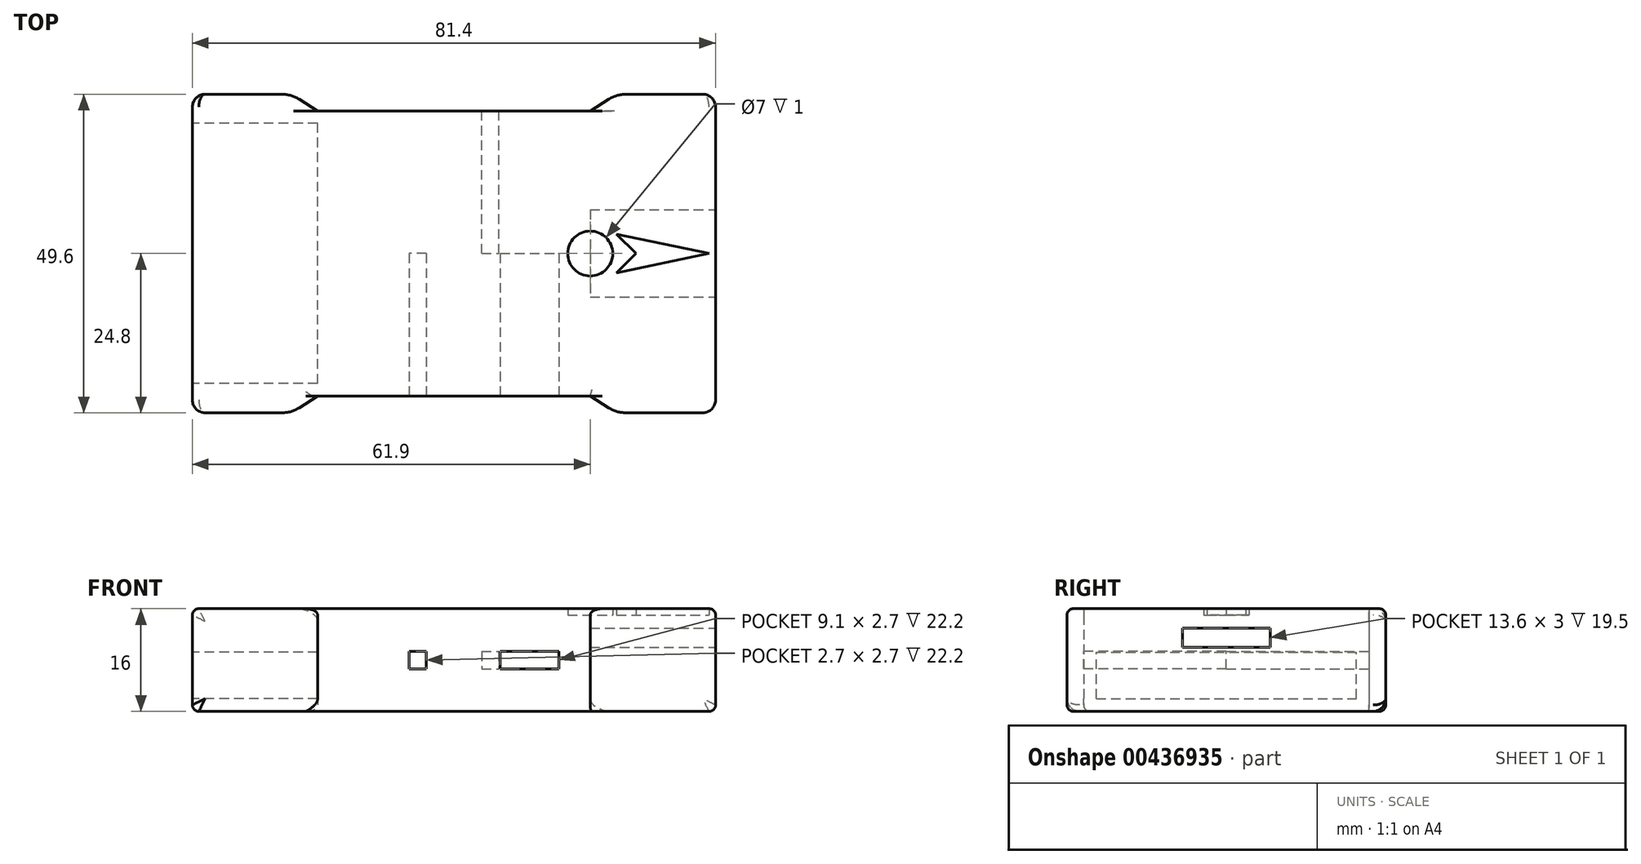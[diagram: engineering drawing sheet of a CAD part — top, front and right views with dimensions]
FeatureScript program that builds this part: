
annotation { "Feature Type Name" : "Feature", "Feature Type Description" : "" }
export const myFeature = defineFeature(function(context is Context, id is Id, definition is map)
    precondition{}
    {
        {
            var Q0;
            Q0=qCreatedBy(makeId("Front.planeOp"),FACE);
            cPlane(context, id + "F0", {"entities" : qUnion([Q0]), "cplaneType" : CPlaneType.OFFSET, "offset" : 22.2 * mm, "width" : 150 * mm, "height" : 150 * mm});
        }
        {
            var Q0;
            Q0=qCreatedBy(makeId("Front.planeOp"),FACE);
            cPlane(context, id + "F1", {"entities" : qUnion([Q0]), "cplaneType" : CPlaneType.OFFSET, "offset" : 22.2 * mm, "oppositeDirection" : true, "width" : 150 * mm, "height" : 150 * mm});
        }
        {
            var Q0;
            Q0=qCreatedBy(makeId("Right.planeOp"),FACE);
            cPlane(context, id + "F2", {"entities" : qUnion([Q0]), "cplaneType" : CPlaneType.OFFSET, "offset" : 40.7 * mm, "width" : 150 * mm, "height" : 150 * mm});
        }
        {
            var Q0;
            Q0=qCreatedBy(makeId("Right.planeOp"),FACE);
            cPlane(context, id + "F3", {"entities" : qUnion([Q0]), "cplaneType" : CPlaneType.OFFSET, "offset" : 40.7 * mm, "oppositeDirection" : true, "width" : 150 * mm, "height" : 150 * mm});
        }
        {
            var Q0;
            Q0=qCreatedBy(makeId("Top.planeOp"),FACE);
            cPlane(context, id + "F4", {"entities" : qUnion([Q0]), "cplaneType" : CPlaneType.OFFSET, "offset" : 13 * mm, "width" : 150 * mm, "height" : 150 * mm});
        }
        {
            var Q0;
            Q0=qCreatedBy(makeId("Top.planeOp"),FACE);
            cPlane(context, id + "F5", {"entities" : qUnion([Q0]), "cplaneType" : CPlaneType.OFFSET, "offset" : 15 * mm, "width" : 150 * mm, "height" : 150 * mm});
        }
        {
            var Q0;
            Q0=qCreatedBy(makeId("Top.planeOp"),FACE);
            var sketch = newSketch(context, id + "F6", { "sketchPlane" : qUnion([Q0])});
            skLineSegment(sketch, "E0.bottom", {"start": v(40.7, -24.8) * mm, "end": v(-40.7, -24.8) * mm, "construction": true});
            skLineSegment(sketch, "E0.top", {"start": v(40.7, 24.8) * mm, "end": v(-40.7, 24.8) * mm, "construction": true});
            skLineSegment(sketch, "E0.left", {"start": v(40.7, -24.8) * mm, "end": v(40.7, 24.8) * mm});
            skLineSegment(sketch, "E0.right", {"start": v(-40.7, -24.8) * mm, "end": v(-40.7, 24.8) * mm});
            skPoint(sketch, "E0.middle", {"position": v(0, 0) * mm});
            skLineSegment(sketch, "E1.bottom", {"start": v(-40.7, 22.2) * mm, "end": v(40.7, 22.2) * mm, "construction": true});
            skLineSegment(sketch, "E1.top", {"start": v(-40.7, -22.2) * mm, "end": v(40.7, -22.2) * mm, "construction": true});
            skLineSegment(sketch, "E2.0", {"start": v(-25.3, -24.8) * mm, "end": v(-25.3, 24.8) * mm, "construction": true});
            skLineSegment(sketch, "E3.0", {"start": v(-21.2, -24.8) * mm, "end": v(-21.2, 24.8) * mm, "construction": true});
            skLineSegment(sketch, "E4", {"start": v(0, 24.8) * mm, "end": v(0, -24.8) * mm, "construction": true});
            skLineSegment(sketch, "E5.MirrorCS", {"start": v(21.2, -24.8) * mm, "end": v(21.2, 24.8) * mm, "construction": true});
            skLineSegment(sketch, "E6.MirrorCS", {"start": v(25.3, -24.8) * mm, "end": v(25.3, 24.8) * mm, "construction": true});
            skLineSegment(sketch, "E7", {"start": v(-25.3, 24.8) * mm, "end": v(-21.2, 22.2) * mm});
            skLineSegment(sketch, "E8", {"start": v(-21.2, 22.2) * mm, "end": v(21.2, 22.2) * mm});
            skLineSegment(sketch, "E9", {"start": v(21.2, 22.2) * mm, "end": v(25.3, 24.8) * mm});
            skLineSegment(sketch, "E10", {"start": v(25.3, 24.8) * mm, "end": v(40.7, 24.8) * mm});
            skLineSegment(sketch, "E11", {"start": v(-25.3, 24.8) * mm, "end": v(-40.7, 24.8) * mm});
            skLineSegment(sketch, "E12", {"start": v(-40.7, -24.8) * mm, "end": v(-25.3, -24.8) * mm});
            skLineSegment(sketch, "E13", {"start": v(-25.3, -24.8) * mm, "end": v(-21.2, -22.2) * mm});
            skLineSegment(sketch, "E14", {"start": v(-21.2, -22.2) * mm, "end": v(21.2, -22.2) * mm});
            skLineSegment(sketch, "E15", {"start": v(21.2, -22.2) * mm, "end": v(25.3, -24.8) * mm});
            skLineSegment(sketch, "E16", {"start": v(25.3, -24.8) * mm, "end": v(40.7, -24.8) * mm});
            skLineSegment(sketch, "E17", {"start": v(-21.2, 22.2) * mm, "end": v(-40.7, 22.2) * mm});
            skLineSegment(sketch, "E18", {"start": v(21.2, 22.2) * mm, "end": v(40.7, 22.2) * mm});
            skLineSegment(sketch, "E19", {"start": v(21.2, -22.2) * mm, "end": v(40.7, -22.2) * mm});
            skLineSegment(sketch, "E20", {"start": v(-21.2, -22.2) * mm, "end": v(-40.7, -22.2) * mm});
            skCircle(sketch, "E21", {"center": v(0, 0) * mm, "radius": 0.5 * mm, "construction": true});
            skSolve(sketch);
        }
        {
            var Q0;
            Q0=qCreatedBy(id+"F0.planeOp",FACE);
            var sketch = newSketch(context, id + "F7", { "sketchPlane" : qUnion([Q0])});
            skLineSegment(sketch, "E22.3", {"start": v(40.7, 0) * mm, "end": v(40.7, 16) * mm});
            skLineSegment(sketch, "E22.6", {"start": v(-40.7, 0) * mm, "end": v(-40.7, 16) * mm});
            skCircle(sketch, "E23", {"center": v(0, 16) * mm, "radius": 0.5 * mm, "construction": true});
            skLineSegment(sketch, "E24", {"start": v(40.7, 0) * mm, "end": v(-40.7, 0) * mm});
            skLineSegment(sketch, "E25", {"start": v(-40.7, 16) * mm, "end": v(40.7, 16) * mm});
            skLineSegment(sketch, "E26", {"start": v(-4.3, 6.65) * mm, "end": v(-7, 6.65) * mm});
            skLineSegment(sketch, "E27.0", {"start": v(-4.3, 9.35) * mm, "end": v(-7, 9.35) * mm});
            skLineSegment(sketch, "E28", {"start": v(-4.3, 6.65) * mm, "end": v(-4.3, 9.35) * mm});
            skLineSegment(sketch, "E29", {"start": v(-7, 6.65) * mm, "end": v(-7, 9.35) * mm});
            skLineSegment(sketch, "E30.0", {"start": v(16.3, 6.65) * mm, "end": v(16.3, 9.35) * mm});
            skLineSegment(sketch, "E31.0", {"start": v(7.2, 6.65) * mm, "end": v(7.2, 9.35) * mm});
            skLineSegment(sketch, "E32", {"start": v(7.2, 6.65) * mm, "end": v(16.3, 6.65) * mm});
            skLineSegment(sketch, "E33", {"start": v(7.2, 9.35) * mm, "end": v(16.3, 9.35) * mm});
            skLineSegment(sketch, "E34.0", {"start": v(21.2, 0) * mm, "end": v(21.2, 16) * mm});
            skLineSegment(sketch, "E35.0", {"start": v(-21.2, 0) * mm, "end": v(-21.2, 16) * mm});
            skLineSegment(sketch, "E36", {"start": v(0, 16) * mm, "end": v(0, 0) * mm, "construction": true});
            skCircle(sketch, "E37", {"center": v(0, 0) * mm, "radius": 0.5 * mm, "construction": true});
            skSolve(sketch);
        }
        {
            var Q0;
            Q0=qCreatedBy(id+"F1.planeOp",FACE);
            var sketch = newSketch(context, id + "F8", { "sketchPlane" : qUnion([Q0])});
            skLineSegment(sketch, "E38.3", {"start": v(-40.7, 16) * mm, "end": v(-40.7, 0) * mm});
            skLineSegment(sketch, "E38.6", {"start": v(40.7, 16) * mm, "end": v(40.7, 0) * mm});
            skLineSegment(sketch, "E39", {"start": v(-40.7, 16) * mm, "end": v(40.7, 16) * mm});
            skLineSegment(sketch, "E40", {"start": v(40.7, 0) * mm, "end": v(-40.7, 0) * mm});
            skLineSegment(sketch, "E41", {"start": v(4.3, 9.35) * mm, "end": v(7, 9.35) * mm});
            skLineSegment(sketch, "E42.0", {"start": v(4.3, 6.65) * mm, "end": v(7, 6.65) * mm});
            skLineSegment(sketch, "E43", {"start": v(4.3, 9.35) * mm, "end": v(4.3, 6.65) * mm});
            skLineSegment(sketch, "E44", {"start": v(7, 9.35) * mm, "end": v(7, 6.65) * mm});
            skCircle(sketch, "E45", {"center": v(0, 16) * mm, "radius": 0.5 * mm, "construction": true});
            skLineSegment(sketch, "E46.0", {"start": v(21.2, 0) * mm, "end": v(21.2, 16) * mm});
            skLineSegment(sketch, "E47.0", {"start": v(-21.2, 0) * mm, "end": v(-21.2, 16) * mm});
            skLineSegment(sketch, "E48", {"start": v(0, 16) * mm, "end": v(0, 0) * mm, "construction": true});
            skCircle(sketch, "E49", {"center": v(0, 0) * mm, "radius": 0.5 * mm, "construction": true});
            skSolve(sketch);
        }
        {
            var Q0;
            Q0=qCreatedBy(id+"F2.planeOp",FACE);
            var sketch = newSketch(context, id + "F9", { "sketchPlane" : qUnion([Q0])});
            skLineSegment(sketch, "E50.0", {"start": v(-24.8, 16) * mm, "end": v(-24.8, 0) * mm});
            skLineSegment(sketch, "E50.1", {"start": v(-22.2, 16) * mm, "end": v(-22.2, 0) * mm});
            skLineSegment(sketch, "E50.2", {"start": v(22.2, 16) * mm, "end": v(22.2, 0) * mm});
            skLineSegment(sketch, "E50.3", {"start": v(24.8, 16) * mm, "end": v(24.8, 0) * mm});
            skCircle(sketch, "E51", {"center": v(0, 0) * mm, "radius": 0.5 * mm, "construction": true});
            skLineSegment(sketch, "E52", {"start": v(-24.8, 16) * mm, "end": v(24.8, 16) * mm});
            skLineSegment(sketch, "E53", {"start": v(24.8, 0) * mm, "end": v(-24.8, 0) * mm});
            skLineSegment(sketch, "E54.0", {"start": v(6.8, 13) * mm, "end": v(6.8, 10) * mm});
            skLineSegment(sketch, "E55.0", {"start": v(-6.8, 13) * mm, "end": v(-6.8, 10) * mm});
            skLineSegment(sketch, "E56.trimOffspring", {"start": v(6.8, 10) * mm, "end": v(-6.8, 10) * mm});
            skLineSegment(sketch, "E57", {"start": v(-22.2, 13) * mm, "end": v(22.2, 13) * mm});
            skSolve(sketch);
        }
        {
            var Q0;
            Q0=qCreatedBy(id+"F3.planeOp",FACE);
            var sketch = newSketch(context, id + "F10", { "sketchPlane" : qUnion([Q0])});
            skLineSegment(sketch, "E58.0", {"start": v(-24.8, 16) * mm, "end": v(-24.8, 0) * mm});
            skLineSegment(sketch, "E58.1", {"start": v(-22.2, 16) * mm, "end": v(-22.2, 0) * mm});
            skLineSegment(sketch, "E58.2", {"start": v(22.2, 16) * mm, "end": v(22.2, 0) * mm});
            skLineSegment(sketch, "E58.3", {"start": v(24.8, 16) * mm, "end": v(24.8, 0) * mm});
            skCircle(sketch, "E59", {"center": v(0, 0) * mm, "radius": 0.5 * mm, "construction": true});
            skLineSegment(sketch, "E60", {"start": v(-24.8, 16) * mm, "end": v(24.8, 16) * mm});
            skLineSegment(sketch, "E61", {"start": v(24.8, 0) * mm, "end": v(-24.8, 0) * mm});
            skLineSegment(sketch, "E62.bottom", {"start": v(-20.25, 2) * mm, "end": v(20.25, 2) * mm});
            skLineSegment(sketch, "E62.top", {"start": v(-20.25, 9.2) * mm, "end": v(20.25, 9.2) * mm});
            skLineSegment(sketch, "E62.left", {"start": v(-20.25, 2) * mm, "end": v(-20.25, 9.2) * mm});
            skLineSegment(sketch, "E62.right", {"start": v(20.25, 2) * mm, "end": v(20.25, 9.2) * mm});
            skSolve(sketch);
        }
        {
            var Q0;
            Q0=qCreatedBy(id+"F4.planeOp",FACE);
            var sketch = newSketch(context, id + "F11", { "sketchPlane" : qUnion([Q0])});
            skLineSegment(sketch, "E63.bottom", {"start": v(40.7, -24.8) * mm, "end": v(-40.7, -24.8) * mm, "construction": true});
            skLineSegment(sketch, "E63.top", {"start": v(40.7, 24.8) * mm, "end": v(-40.7, 24.8) * mm, "construction": true});
            skLineSegment(sketch, "E63.left", {"start": v(40.7, -24.8) * mm, "end": v(40.7, 24.8) * mm});
            skLineSegment(sketch, "E63.right", {"start": v(-40.7, -24.8) * mm, "end": v(-40.7, 24.8) * mm});
            skPoint(sketch, "E63.middle", {"position": v(0, 0) * mm});
            skLineSegment(sketch, "E64.bottom", {"start": v(-40.7, 22.2) * mm, "end": v(40.7, 22.2) * mm, "construction": true});
            skLineSegment(sketch, "E64.top", {"start": v(-40.7, -22.2) * mm, "end": v(40.7, -22.2) * mm, "construction": true});
            skLineSegment(sketch, "E65.0", {"start": v(-25.3, -24.8) * mm, "end": v(-25.3, 24.8) * mm, "construction": true});
            skLineSegment(sketch, "E66.0", {"start": v(-21.2, -24.8) * mm, "end": v(-21.2, 24.8) * mm, "construction": true});
            skLineSegment(sketch, "E67", {"start": v(0, 24.8) * mm, "end": v(0, -24.8) * mm, "construction": true});
            skLineSegment(sketch, "E68.MirrorCS", {"start": v(21.2, -24.8) * mm, "end": v(21.2, 24.8) * mm, "construction": true});
            skLineSegment(sketch, "E69.MirrorCS", {"start": v(25.3, -24.8) * mm, "end": v(25.3, 24.8) * mm, "construction": true});
            skLineSegment(sketch, "E70", {"start": v(-25.3, 24.8) * mm, "end": v(-21.2, 22.2) * mm});
            skLineSegment(sketch, "E71", {"start": v(-21.2, 22.2) * mm, "end": v(21.2, 22.2) * mm});
            skLineSegment(sketch, "E72", {"start": v(21.2, 22.2) * mm, "end": v(25.3, 24.8) * mm});
            skLineSegment(sketch, "E73", {"start": v(25.3, 24.8) * mm, "end": v(40.7, 24.8) * mm});
            skLineSegment(sketch, "E74", {"start": v(-25.3, 24.8) * mm, "end": v(-40.7, 24.8) * mm});
            skLineSegment(sketch, "E75", {"start": v(-40.7, -24.8) * mm, "end": v(-25.3, -24.8) * mm});
            skLineSegment(sketch, "E76", {"start": v(-25.3, -24.8) * mm, "end": v(-21.2, -22.2) * mm});
            skLineSegment(sketch, "E77", {"start": v(-21.2, -22.2) * mm, "end": v(21.2, -22.2) * mm});
            skLineSegment(sketch, "E78", {"start": v(21.2, -22.2) * mm, "end": v(25.3, -24.8) * mm});
            skLineSegment(sketch, "E79", {"start": v(25.3, -24.8) * mm, "end": v(40.7, -24.8) * mm});
            skLineSegment(sketch, "E80", {"start": v(-21.2, 22.2) * mm, "end": v(-40.7, 22.2) * mm});
            skLineSegment(sketch, "E81", {"start": v(21.2, 22.2) * mm, "end": v(40.7, 22.2) * mm});
            skLineSegment(sketch, "E82", {"start": v(21.2, -22.2) * mm, "end": v(40.7, -22.2) * mm});
            skLineSegment(sketch, "E83", {"start": v(-21.2, -22.2) * mm, "end": v(-40.7, -22.2) * mm});
            skLineSegment(sketch, "E84", {"start": v(25.3, 3) * mm, "end": v(39.7, 0) * mm});
            skLineSegment(sketch, "E85", {"start": v(25.3, -3) * mm, "end": v(39.7, 0) * mm});
            skLineSegment(sketch, "E86", {"start": v(25.3, 3) * mm, "end": v(28.3, 0) * mm});
            skLineSegment(sketch, "E87", {"start": v(28.3, 0) * mm, "end": v(25.3, -3) * mm});
            skSolve(sketch);
        }
        {
            var Q0;
            Q0=qCreatedBy(id+"F5.planeOp",FACE);
            var sketch = newSketch(context, id + "F12", { "sketchPlane" : qUnion([Q0])});
            skCircle(sketch, "E88", {"center": v(21.2, 0) * mm, "radius": 4.1 * mm, "construction": true});
            skCircle(sketch, "E89", {"center": v(0, 0) * mm, "radius": 0.5 * mm, "construction": true});
            skSolve(sketch);
        }
        {
            var Q0;
            Q0=makeQuery(id+"F7.imprint","IMPRINT",FACE,{"disambiguationData":[TD([[makeQuery(id+"F7.imprint","IMPRINT",EDGE,{"derivedFrom":sQuery(id+"F7.wireOp",EDGE,"E26")}),1.0]])]});
            extrude(context, id + "F13", {"entities" : qUnion([Q0]), "oppositeDirection" : true, "depth" : 22.2 * mm});
        }
        {
            var Q0;
            Q0=makeQuery(id+"F8.imprint","IMPRINT",FACE,{"disambiguationData":[TD([[makeQuery(id+"F8.imprint","IMPRINT",EDGE,{"derivedFrom":sQuery(id+"F8.wireOp",EDGE,"E41")}),1.0]])]});
            extrude(context, id + "F14", {"entities" : qUnion([Q0]), "operationType" : NewBodyOperationType.ADD, "depth" : 22.2 * mm});
        }
        {
            var Q0;
            {var subQ9=sQuery(id+"F9.wireOp",EDGE,"E54.0");Q0=makeQuery(id+"F9.imprint","IMPRINT",FACE,{"disambiguationData":[TD([[makeQuery(id+"F9.imprint","IMPRINT",EDGE,{"derivedFrom":subQ9}),1.0]])]});}
            extrude(context, id + "F15", {"entities" : qUnion([Q0]), "operationType" : NewBodyOperationType.ADD, "oppositeDirection" : true, "depth" : 19.5 * mm});
        }
        {
            var Q0;
            {var subQ0=sQuery(id+"F10.wireOp",EDGE,"E58.1");Q0=makeQuery(id+"F10.imprint","IMPRINT",FACE,{"disambiguationData":[TD([[makeQuery(id+"F10.imprint","IMPRINT",EDGE,{"derivedFrom":subQ0}),1.0]])]});}
            extrude(context, id + "F16", {"entities" : qUnion([Q0]), "operationType" : NewBodyOperationType.ADD, "depth" : 19.5 * mm});
        }
        {
            var Q0;
            Q0=makeQuery(id+"F11.imprint","IMPRINT",FACE,{"disambiguationData":[TD([[makeQuery(id+"F11.imprint","IMPRINT",EDGE,{"derivedFrom":sQuery(id+"F11.wireOp",EDGE,"E71")}),-1.0]])]});
            extrude(context, id + "F17", {"entities" : qUnion([Q0]), "operationType" : NewBodyOperationType.ADD, "depth" : 3 * mm});
        }
        {
            var Q0;
            Q0=makeQuery(id+"F11.imprint","IMPRINT",FACE,{"disambiguationData":[TD([[makeQuery(id+"F11.imprint","IMPRINT",EDGE,{"derivedFrom":sQuery(id+"F11.wireOp",EDGE,"E84")}),-1.0]])]});
            extrude(context, id + "F18", {"entities" : qUnion([Q0]), "operationType" : NewBodyOperationType.ADD, "depth" : 2 * mm});
        }
        {
            var Q0;
            Q0=makeQuery(id+"F6.imprint","IMPRINT",FACE,{"disambiguationData":[TD([[makeQuery(id+"F6.imprint","IMPRINT",EDGE,{"derivedFrom":sQuery(id+"F6.wireOp",EDGE,"E15")}),1.0]])]});
            var Q1;
            {var subQ0=sQuery(id+"F6.wireOp",EDGE,"E12");Q1=makeQuery(id+"F6.imprint","IMPRINT",FACE,{"disambiguationData":[TD([[makeQuery(id+"F6.imprint","IMPRINT",EDGE,{"derivedFrom":subQ0}),1.0]])]});}
            var Q2;
            Q2=makeQuery(id+"F6.imprint","IMPRINT",FACE,{"disambiguationData":[TD([[makeQuery(id+"F6.imprint","IMPRINT",EDGE,{"derivedFrom":sQuery(id+"F6.wireOp",EDGE,"E7")}),-1.0]])]});
            var Q3;
            Q3=makeQuery(id+"F6.imprint","IMPRINT",FACE,{"disambiguationData":[TD([[makeQuery(id+"F6.imprint","IMPRINT",EDGE,{"derivedFrom":sQuery(id+"F6.wireOp",EDGE,"E9")}),-1.0]])]});
            extrude(context, id + "F19", {"entities" : qUnion([Q0, Q1, Q2, Q3]), "operationType" : NewBodyOperationType.ADD, "depth" : 16 * mm});
        }
        {
            var Q0;
            Q0=makeQuery(id+"F19.opExtrude","SWEPT_EDGE",EDGE,{"disambiguationData":[OSD([sQuery(id+"F6.wireOp",EDGE,"E13"),sQuery(id+"F6.wireOp",EDGE,"E14"),sQuery(id+"F6.wireOp",EDGE,"E20")])]});
            var Q1;
            Q1=makeQuery(id+"F19.opExtrude","SWEPT_EDGE",EDGE,{"disambiguationData":[OSD([sQuery(id+"F6.wireOp",EDGE,"E12"),sQuery(id+"F6.wireOp",EDGE,"E13")])]});
            var Q2;
            Q2=makeQuery(id+"F19.opExtrude","SWEPT_EDGE",EDGE,{"disambiguationData":[OSD([sQuery(id+"F6.wireOp",EDGE,"E15"),sQuery(id+"F6.wireOp",EDGE,"E16")])]});
            var Q3;
            Q3=makeQuery(id+"F19.opExtrude","SWEPT_EDGE",EDGE,{"disambiguationData":[OSD([sQuery(id+"F6.wireOp",EDGE,"E9"),sQuery(id+"F6.wireOp",EDGE,"E10")])]});
            var Q4;
            Q4=makeQuery(id+"F19.opExtrude","SWEPT_EDGE",EDGE,{"disambiguationData":[OSD([sQuery(id+"F6.wireOp",EDGE,"E8"),sQuery(id+"F6.wireOp",EDGE,"E9"),sQuery(id+"F6.wireOp",EDGE,"E18")])]});
            var Q5;
            Q5=makeQuery(id+"F19.opExtrude","SWEPT_EDGE",EDGE,{"disambiguationData":[OSD([sQuery(id+"F6.wireOp",EDGE,"E7"),sQuery(id+"F6.wireOp",EDGE,"E8"),sQuery(id+"F6.wireOp",EDGE,"E17")])]});
            var Q6;
            Q6=makeQuery(id+"F19.opExtrude","SWEPT_EDGE",EDGE,{"disambiguationData":[OSD([sQuery(id+"F6.wireOp",EDGE,"E7"),sQuery(id+"F6.wireOp",EDGE,"E11")])]});
            fillet(context, id + "F20", {"entities" : qUnion([Q0, Q1, Q2, Q3, Q4, Q5, Q6]), "radius" : 5 * mm, "tangentPropagation" : true, "allowEdgeOverflow" : false});
        }
        {
            var Q0;
            {var subQ0=sQuery(id+"F6.wireOp",EDGE,"E0.left");Q0=makeQuery(id+"F19.boolean.opBoolean","MERGE",EDGE,{"derivedFrom":[makeQuery(id+"F17.opExtrude","CAP_EDGE",EDGE,{"disambiguationData":[OSD([sQuery(id+"F11.wireOp",EDGE,"E63.left")])],"isStart":false}),makeQuery(id+"F19.opExtrude","CAP_EDGE",EDGE,{"disambiguationData":[OSD([subQ0]),TDD([makeQuery(id+"F6.imprint","IMPRINT",EDGE,{"disambiguationData":[TD([[makeQuery(id+"F6.imprint","INTERSECT",VERTEX,{"derivedFrom":[subQ0,sQuery(id+"F6.wireOp",EDGE,"E16")]}),-1.0]])],"derivedFrom":subQ0})])],"isStart":false}),makeQuery(id+"F19.opExtrude","CAP_EDGE",EDGE,{"disambiguationData":[OSD([subQ0]),TDD([makeQuery(id+"F6.imprint","IMPRINT",EDGE,{"disambiguationData":[TD([[makeQuery(id+"F6.imprint","INTERSECT",VERTEX,{"derivedFrom":[subQ0,sQuery(id+"F6.wireOp",EDGE,"E10")]}),1.0]])],"derivedFrom":subQ0})])],"isStart":false})]});}
            var Q1;
            Q1=makeQuery(id+"F19.opExtrude","CAP_EDGE",EDGE,{"disambiguationData":[OSD([sQuery(id+"F6.wireOp",EDGE,"E10")])],"isStart":false});
            var Q2;
            {var subQ0=sQuery(id+"F6.wireOp",EDGE,"E0.right");var subQ1=sQuery(id+"F6.wireOp",EDGE,"E10");var subQ2=sQuery(id+"F6.wireOp",EDGE,"E9");var subQ3=sQuery(id+"F6.wireOp",EDGE,"E0.left");Q2=makeQuery(id+"F20.opFillet","BLEND_EDGE",EDGE,{"blendedFrom":[makeQuery(id+"F19.opExtrude","SWEPT_EDGE",EDGE,{"disambiguationData":[OSD([subQ2,subQ1])]}),makeQuery(id+"F19.boolean.opBoolean","MERGE",FACE,{"derivedFrom":[makeQuery(id+"F17.boolean.opBoolean","MERGE",FACE,{"derivedFrom":[makeQuery(id+"F16.boolean.opBoolean","MERGE",FACE,{"derivedFrom":[makeQuery(id+"F14.boolean.opBoolean","MERGE",FACE,{"derivedFrom":[makeQuery(id+"F13.opExtrude","SWEPT_FACE",FACE,{"disambiguationData":[OSD([sQuery(id+"F7.wireOp",EDGE,"E25")])]}),makeQuery(id+"F14.opExtrude","SWEPT_FACE",FACE,{"disambiguationData":[OSD([sQuery(id+"F8.wireOp",EDGE,"E39")])]})]}),makeQuery(id+"F16.opExtrude","SWEPT_FACE",FACE,{"disambiguationData":[OSD([sQuery(id+"F10.wireOp",EDGE,"E60")])]})]}),makeQuery(id+"F17.opExtrude","CAP_FACE",FACE,{"disambiguationData":[OSD([sQuery(id+"F11.wireOp",EDGE,"E63.left"),sQuery(id+"F11.wireOp",EDGE,"E63.right"),sQuery(id+"F11.wireOp",EDGE,"E71"),sQuery(id+"F11.wireOp",EDGE,"E77"),sQuery(id+"F11.wireOp",EDGE,"E80"),sQuery(id+"F11.wireOp",EDGE,"E81"),sQuery(id+"F11.wireOp",EDGE,"E82"),sQuery(id+"F11.wireOp",EDGE,"E83"),sQuery(id+"F11.wireOp",EDGE,"E84"),sQuery(id+"F11.wireOp",EDGE,"E85"),sQuery(id+"F11.wireOp",EDGE,"E86"),sQuery(id+"F11.wireOp",EDGE,"E87")])],"isStart":false})]}),makeQuery(id+"F19.opExtrude","CAP_FACE",FACE,{"disambiguationData":[OSD([subQ3,sQuery(id+"F6.wireOp",EDGE,"E15"),sQuery(id+"F6.wireOp",EDGE,"E16"),sQuery(id+"F6.wireOp",EDGE,"E19")])],"isStart":false}),makeQuery(id+"F19.opExtrude","CAP_FACE",FACE,{"disambiguationData":[OSD([subQ3,subQ2,subQ1,sQuery(id+"F6.wireOp",EDGE,"E18")])],"isStart":false}),makeQuery(id+"F19.opExtrude","CAP_FACE",FACE,{"disambiguationData":[OSD([subQ0,sQuery(id+"F6.wireOp",EDGE,"E12"),sQuery(id+"F6.wireOp",EDGE,"E13"),sQuery(id+"F6.wireOp",EDGE,"E20")])],"isStart":false}),makeQuery(id+"F19.opExtrude","CAP_FACE",FACE,{"disambiguationData":[OSD([subQ0,sQuery(id+"F6.wireOp",EDGE,"E7"),sQuery(id+"F6.wireOp",EDGE,"E11"),sQuery(id+"F6.wireOp",EDGE,"E17")])],"isStart":false})]})],"blendedInto":[makeQuery(id+"F19.boolean.opBoolean","MERGE",FACE,{"derivedFrom":[makeQuery(id+"F17.boolean.opBoolean","MERGE",FACE,{"derivedFrom":[makeQuery(id+"F16.boolean.opBoolean","MERGE",FACE,{"derivedFrom":[makeQuery(id+"F14.boolean.opBoolean","MERGE",FACE,{"derivedFrom":[makeQuery(id+"F13.opExtrude","SWEPT_FACE",FACE,{"disambiguationData":[OSD([sQuery(id+"F7.wireOp",EDGE,"E25")])]}),makeQuery(id+"F14.opExtrude","SWEPT_FACE",FACE,{"disambiguationData":[OSD([sQuery(id+"F8.wireOp",EDGE,"E39")])]})]}),makeQuery(id+"F16.opExtrude","SWEPT_FACE",FACE,{"disambiguationData":[OSD([sQuery(id+"F10.wireOp",EDGE,"E60")])]})]}),makeQuery(id+"F17.opExtrude","CAP_FACE",FACE,{"disambiguationData":[OSD([sQuery(id+"F11.wireOp",EDGE,"E63.left"),sQuery(id+"F11.wireOp",EDGE,"E63.right"),sQuery(id+"F11.wireOp",EDGE,"E71"),sQuery(id+"F11.wireOp",EDGE,"E77"),sQuery(id+"F11.wireOp",EDGE,"E80"),sQuery(id+"F11.wireOp",EDGE,"E81"),sQuery(id+"F11.wireOp",EDGE,"E82"),sQuery(id+"F11.wireOp",EDGE,"E83"),sQuery(id+"F11.wireOp",EDGE,"E84"),sQuery(id+"F11.wireOp",EDGE,"E85"),sQuery(id+"F11.wireOp",EDGE,"E86"),sQuery(id+"F11.wireOp",EDGE,"E87")])],"isStart":false})]}),makeQuery(id+"F19.opExtrude","CAP_FACE",FACE,{"disambiguationData":[OSD([subQ3,sQuery(id+"F6.wireOp",EDGE,"E15"),sQuery(id+"F6.wireOp",EDGE,"E16"),sQuery(id+"F6.wireOp",EDGE,"E19")])],"isStart":false}),makeQuery(id+"F19.opExtrude","CAP_FACE",FACE,{"disambiguationData":[OSD([subQ3,subQ2,subQ1,sQuery(id+"F6.wireOp",EDGE,"E18")])],"isStart":false}),makeQuery(id+"F19.opExtrude","CAP_FACE",FACE,{"disambiguationData":[OSD([subQ0,sQuery(id+"F6.wireOp",EDGE,"E12"),sQuery(id+"F6.wireOp",EDGE,"E13"),sQuery(id+"F6.wireOp",EDGE,"E20")])],"isStart":false}),makeQuery(id+"F19.opExtrude","CAP_FACE",FACE,{"disambiguationData":[OSD([subQ0,sQuery(id+"F6.wireOp",EDGE,"E7"),sQuery(id+"F6.wireOp",EDGE,"E11"),sQuery(id+"F6.wireOp",EDGE,"E17")])],"isStart":false})]})]});}
            var Q3;
            {var subQ0=sQuery(id+"F6.wireOp",EDGE,"E0.right");Q3=makeQuery(id+"F19.boolean.opBoolean","MERGE",EDGE,{"derivedFrom":[makeQuery(id+"F16.opExtrude","CAP_EDGE",EDGE,{"disambiguationData":[OSD([sQuery(id+"F10.wireOp",EDGE,"E60")])],"isStart":true}),makeQuery(id+"F19.opExtrude","CAP_EDGE",EDGE,{"disambiguationData":[OSD([subQ0]),TDD([makeQuery(id+"F6.imprint","IMPRINT",EDGE,{"disambiguationData":[TD([[makeQuery(id+"F6.imprint","INTERSECT",VERTEX,{"derivedFrom":[subQ0,sQuery(id+"F6.wireOp",EDGE,"E12")]}),-1.0]])],"derivedFrom":subQ0})])],"isStart":false}),makeQuery(id+"F19.opExtrude","CAP_EDGE",EDGE,{"disambiguationData":[OSD([subQ0]),TDD([makeQuery(id+"F6.imprint","IMPRINT",EDGE,{"disambiguationData":[TD([[makeQuery(id+"F6.imprint","INTERSECT",VERTEX,{"derivedFrom":[subQ0,sQuery(id+"F6.wireOp",EDGE,"E11")]}),1.0]])],"derivedFrom":subQ0})])],"isStart":false})]});}
            var Q4;
            Q4=makeQuery(id+"F19.opExtrude","CAP_EDGE",EDGE,{"disambiguationData":[OSD([sQuery(id+"F6.wireOp",EDGE,"E12")])],"isStart":false});
            var Q5;
            Q5=makeQuery(id+"F19.opExtrude","CAP_EDGE",EDGE,{"disambiguationData":[OSD([sQuery(id+"F6.wireOp",EDGE,"E16")])],"isStart":false});
            var Q6;
            Q6=makeQuery(id+"F19.opExtrude","CAP_EDGE",EDGE,{"disambiguationData":[OSD([sQuery(id+"F6.wireOp",EDGE,"E11")])],"isStart":true});
            var Q7;
            Q7=makeQuery(id+"F19.opExtrude","CAP_EDGE",EDGE,{"disambiguationData":[OSD([sQuery(id+"F6.wireOp",EDGE,"E7")])],"isStart":true});
            var Q8;
            Q8=makeQuery(id+"F19.opExtrude","CAP_EDGE",EDGE,{"disambiguationData":[OSD([sQuery(id+"F6.wireOp",EDGE,"E16")])],"isStart":true});
            var Q9;
            Q9=makeQuery(id+"F16.boolean.opBoolean","MERGE",EDGE,{"derivedFrom":[makeQuery(id+"F15.boolean.opBoolean","MERGE",EDGE,{"derivedFrom":[makeQuery(id+"F13.opExtrude","CAP_EDGE",EDGE,{"disambiguationData":[OSD([sQuery(id+"F7.wireOp",EDGE,"E24")])],"isStart":true}),makeQuery(id+"F15.opExtrude","SWEPT_EDGE",EDGE,{"disambiguationData":[OSD([sQuery(id+"F9.wireOp",EDGE,"E50.1"),sQuery(id+"F9.wireOp",EDGE,"E53")])]})]}),makeQuery(id+"F16.opExtrude","SWEPT_EDGE",EDGE,{"disambiguationData":[OSD([sQuery(id+"F10.wireOp",EDGE,"E58.1"),sQuery(id+"F10.wireOp",EDGE,"E61")])]})]});
            var Q10;
            {var subQ0=sQuery(id+"F6.wireOp",EDGE,"E0.right");Q10=makeQuery(id+"F19.boolean.opBoolean","MERGE",EDGE,{"derivedFrom":[makeQuery(id+"F16.opExtrude","CAP_EDGE",EDGE,{"disambiguationData":[OSD([sQuery(id+"F10.wireOp",EDGE,"E61")])],"isStart":true}),makeQuery(id+"F19.opExtrude","CAP_EDGE",EDGE,{"disambiguationData":[OSD([subQ0]),TDD([makeQuery(id+"F6.imprint","IMPRINT",EDGE,{"disambiguationData":[TD([[makeQuery(id+"F6.imprint","INTERSECT",VERTEX,{"derivedFrom":[subQ0,sQuery(id+"F6.wireOp",EDGE,"E12")]}),-1.0]])],"derivedFrom":subQ0})])],"isStart":true}),makeQuery(id+"F19.opExtrude","CAP_EDGE",EDGE,{"disambiguationData":[OSD([subQ0]),TDD([makeQuery(id+"F6.imprint","IMPRINT",EDGE,{"disambiguationData":[TD([[makeQuery(id+"F6.imprint","INTERSECT",VERTEX,{"derivedFrom":[subQ0,sQuery(id+"F6.wireOp",EDGE,"E11")]}),1.0]])],"derivedFrom":subQ0})])],"isStart":true})]});}
            var Q11;
            {var subQ0=sQuery(id+"F6.wireOp",EDGE,"E0.left");Q11=makeQuery(id+"F19.boolean.opBoolean","MERGE",EDGE,{"derivedFrom":[makeQuery(id+"F15.opExtrude","CAP_EDGE",EDGE,{"disambiguationData":[OSD([sQuery(id+"F9.wireOp",EDGE,"E53")])],"isStart":true}),makeQuery(id+"F19.opExtrude","CAP_EDGE",EDGE,{"disambiguationData":[OSD([subQ0]),TDD([makeQuery(id+"F6.imprint","IMPRINT",EDGE,{"disambiguationData":[TD([[makeQuery(id+"F6.imprint","INTERSECT",VERTEX,{"derivedFrom":[subQ0,sQuery(id+"F6.wireOp",EDGE,"E16")]}),-1.0]])],"derivedFrom":subQ0})])],"isStart":true}),makeQuery(id+"F19.opExtrude","CAP_EDGE",EDGE,{"disambiguationData":[OSD([subQ0]),TDD([makeQuery(id+"F6.imprint","IMPRINT",EDGE,{"disambiguationData":[TD([[makeQuery(id+"F6.imprint","INTERSECT",VERTEX,{"derivedFrom":[subQ0,sQuery(id+"F6.wireOp",EDGE,"E10")]}),1.0]])],"derivedFrom":subQ0})])],"isStart":true})]});}
            fillet(context, id + "F21", {"entities" : qUnion([Q0, Q1, Q2, Q3, Q4, Q5, Q6, Q7, Q8, Q9, Q10, Q11]), "radius" : 1 * mm, "tangentPropagation" : true, "allowEdgeOverflow" : false});
        }
        {
            var Q0;
            Q0=makeQuery(id+"F19.opExtrude","SWEPT_EDGE",EDGE,{"disambiguationData":[OSD([sQuery(id+"F6.wireOp",EDGE,"E0.right"),sQuery(id+"F6.wireOp",EDGE,"E12")])]});
            var Q1;
            Q1=makeQuery(id+"F19.opExtrude","SWEPT_EDGE",EDGE,{"disambiguationData":[OSD([sQuery(id+"F6.wireOp",EDGE,"E0.right"),sQuery(id+"F6.wireOp",EDGE,"E11")])]});
            var Q2;
            Q2=makeQuery(id+"F19.opExtrude","SWEPT_EDGE",EDGE,{"disambiguationData":[OSD([sQuery(id+"F6.wireOp",EDGE,"E0.left"),sQuery(id+"F6.wireOp",EDGE,"E10")])]});
            var Q3;
            Q3=makeQuery(id+"F19.opExtrude","SWEPT_EDGE",EDGE,{"disambiguationData":[OSD([sQuery(id+"F6.wireOp",EDGE,"E0.left"),sQuery(id+"F6.wireOp",EDGE,"E16")])]});
            fillet(context, id + "F22", {"entities" : qUnion([Q0, Q1, Q2, Q3]), "radius" : 2 * mm, "tangentPropagation" : true, "allowEdgeOverflow" : false});
        }
        {
            var Q0;
            Q0=sQuery(id+"F12.wireOp",VERTEX,"E88.center");
            var Q1;
            Q1=makeQuery(id+"F13.opExtrude","SWEPT_BODY",BODY,{"disambiguationData":[OSD([sQuery(id+"F7.wireOp",EDGE,"E24"),sQuery(id+"F7.wireOp",EDGE,"E25"),sQuery(id+"F7.wireOp",EDGE,"E26"),sQuery(id+"F7.wireOp",EDGE,"E27.0"),sQuery(id+"F7.wireOp",EDGE,"E28"),sQuery(id+"F7.wireOp",EDGE,"E29"),sQuery(id+"F7.wireOp",EDGE,"E30.0"),sQuery(id+"F7.wireOp",EDGE,"E31.0"),sQuery(id+"F7.wireOp",EDGE,"E32"),sQuery(id+"F7.wireOp",EDGE,"E33"),sQuery(id+"F7.wireOp",EDGE,"E34.0"),sQuery(id+"F7.wireOp",EDGE,"E35.0")])]});
            hole(context, id + "F23", {"style" : HoleStyle.SIMPLE, "endStyle" : HoleEndStyle.BLIND, "oppositeDirection" : true, "holeDiameter" : 7 * mm, "holeDepth" : 2 * mm, "isTappedThrough" : true, "tappedDepth" : 12 * mm, "tapClearance" : 3, "startFromSketch" : true, "locations" : qUnion([Q0]), "scope" : qUnion([Q1])});
        }
    });
